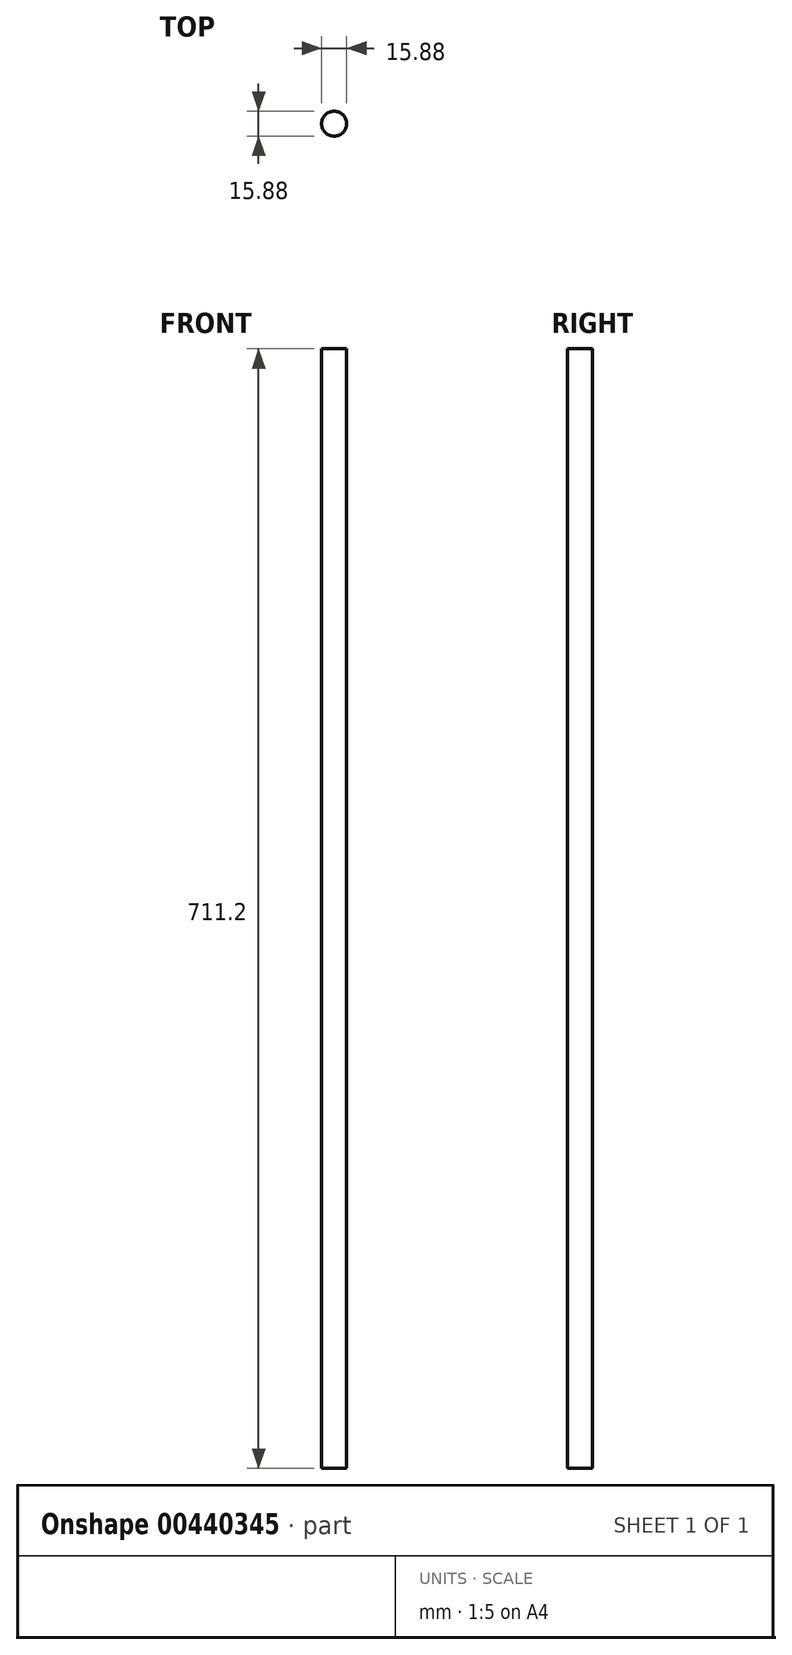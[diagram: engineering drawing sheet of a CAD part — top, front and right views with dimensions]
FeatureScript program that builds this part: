
annotation { "Feature Type Name" : "Feature", "Feature Type Description" : "" }
export const myFeature = defineFeature(function(context is Context, id is Id, definition is map)
    precondition{}
    {
        {
            var Q0;
            Q0=qCreatedBy(makeId("Top.planeOp"),FACE);
            var sketch = newSketch(context, id + "F0", { "sketchPlane" : qUnion([Q0])});
            skCircle(sketch, "E0", {"center": v(0, 0) * mm, "radius": 7.94 * mm});
            skSolve(sketch);
        }
        {
            var Q0;
            Q0=makeQuery(id+"F0.imprint","IMPRINT",FACE,{"disambiguationData":[TD([[makeQuery(id+"F0.imprint","IMPRINT",EDGE,{"derivedFrom":sQuery(id+"F0.wireOp",EDGE,"E0")}),1.0]])]});
            extrude(context, id + "F1", {"entities" : qUnion([Q0]), "endBound" : BoundingType.SYMMETRIC, "depth" : 711.2 * mm});
        }
    });
